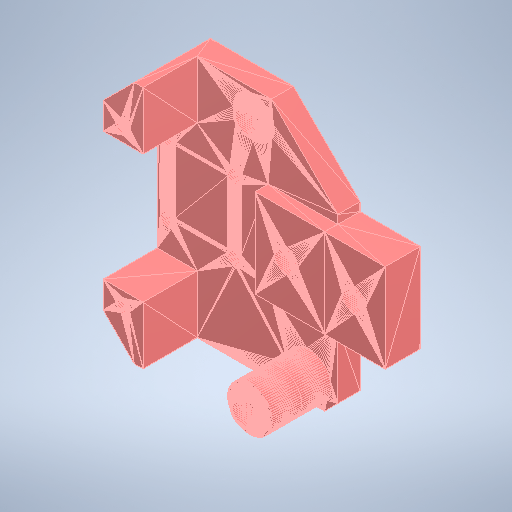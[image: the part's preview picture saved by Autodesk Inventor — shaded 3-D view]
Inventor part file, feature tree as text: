
AUTODESK INVENTOR PART (.ipt)
format: ipt  version: 2025.2 (Build 292293000, 293)  size: 331,776 bytes
history: native  units: in
note: dims shown in document units (in); Inventor stores cm internally (conversion verified against a paired STEP export)
features: other x2, plane x1
ambient origin geometry x8: Origin, YZ Plane, XZ Plane, XY Plane, X Axis, Y Axis, Z Axis, Center Point
feature tree (3):
  other  "1 X Left_Y_Carriage_Bottom"
  plane  "Work Plane1"
  other  "MeshFeature1"
